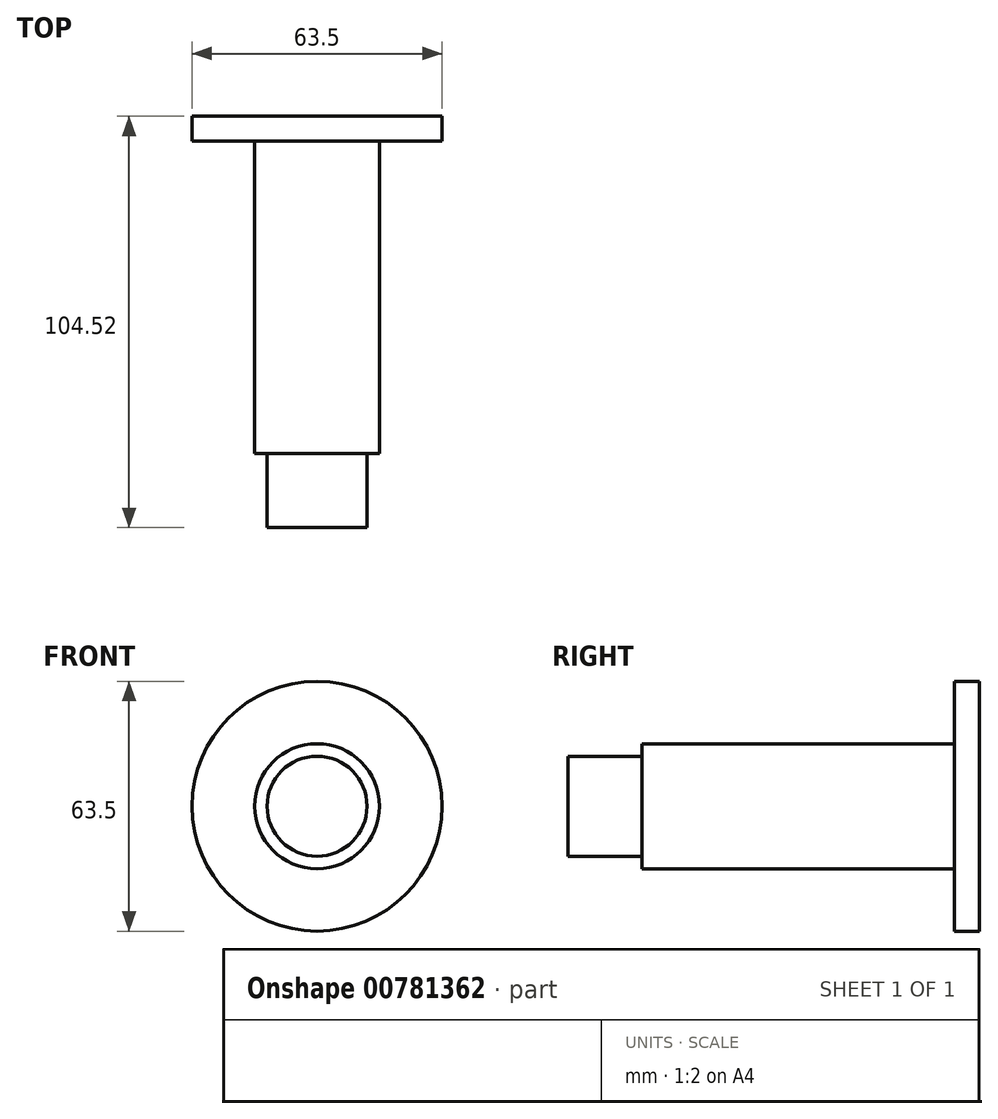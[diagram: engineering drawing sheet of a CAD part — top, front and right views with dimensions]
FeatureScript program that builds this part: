
annotation { "Feature Type Name" : "Feature", "Feature Type Description" : "" }
export const myFeature = defineFeature(function(context is Context, id is Id, definition is map)
    precondition{}
    {
        {
            var Q0;
            Q0=qCreatedBy(makeId("Right.planeOp"),FACE);
            var sketch = newSketch(context, id + "F0", { "sketchPlane" : qUnion([Q0])});
            skLineSegment(sketch, "E0.bottom", {"start": v(0, 0) * mm, "end": v(18.8, 0) * mm});
            skLineSegment(sketch, "E0.top", {"start": v(0, 12.7) * mm, "end": v(18.8, 12.7) * mm});
            skLineSegment(sketch, "E0.left", {"start": v(0, 0) * mm, "end": v(0, 12.7) * mm});
            skLineSegment(sketch, "E0.right", {"start": v(18.8, 0) * mm, "end": v(18.8, 12.7) * mm});
            skLineSegment(sketch, "E1.bottom", {"start": v(18.8, 0) * mm, "end": v(98.17, 0) * mm});
            skLineSegment(sketch, "E1.top", {"start": v(18.8, 15.88) * mm, "end": v(98.17, 15.88) * mm});
            skLineSegment(sketch, "E1.left", {"start": v(18.8, 0) * mm, "end": v(18.8, 15.88) * mm});
            skLineSegment(sketch, "E1.right", {"start": v(98.17, 0) * mm, "end": v(98.17, 15.88) * mm});
            skLineSegment(sketch, "E2.bottom", {"start": v(98.17, 0) * mm, "end": v(104.52, 0) * mm});
            skLineSegment(sketch, "E2.top", {"start": v(98.17, 31.75) * mm, "end": v(104.52, 31.75) * mm});
            skLineSegment(sketch, "E2.left", {"start": v(98.17, 0) * mm, "end": v(98.17, 31.75) * mm});
            skLineSegment(sketch, "E2.right", {"start": v(104.52, 0) * mm, "end": v(104.52, 31.75) * mm});
            skSolve(sketch);
        }
        {
            var Q0;
            {var subQ0=sQuery(id+"F0.wireOp",EDGE,"E0.bottom");Q0=makeQuery(id+"F0.imprint","IMPRINT",FACE,{"disambiguationData":[TD([[makeQuery(id+"F0.imprint","IMPRINT",EDGE,{"derivedFrom":subQ0}),1.0]])]});}
            var Q1;
            {var subQ3=sQuery(id+"F0.wireOp",EDGE,"E1.bottom");Q1=makeQuery(id+"F0.imprint","IMPRINT",FACE,{"disambiguationData":[TD([[makeQuery(id+"F0.imprint","IMPRINT",EDGE,{"derivedFrom":subQ3}),1.0]])]});}
            var Q2;
            {var subQ3=sQuery(id+"F0.wireOp",EDGE,"E2.bottom");Q2=makeQuery(id+"F0.imprint","IMPRINT",FACE,{"disambiguationData":[TD([[makeQuery(id+"F0.imprint","IMPRINT",EDGE,{"derivedFrom":subQ3}),1.0]])]});}
            var Q3;
            Q3=sQuery(id+"F0.wireOp",EDGE,"E1.bottom");
            revolve(context, id + "F1", {"surfaceOperationType" : NewSurfaceOperationType.NEW, "entities" : qUnion([Q0, Q1, Q2]), "axis" : qUnion([Q3]), "revolveType" : RevolveType.FULL});
        }
    });
